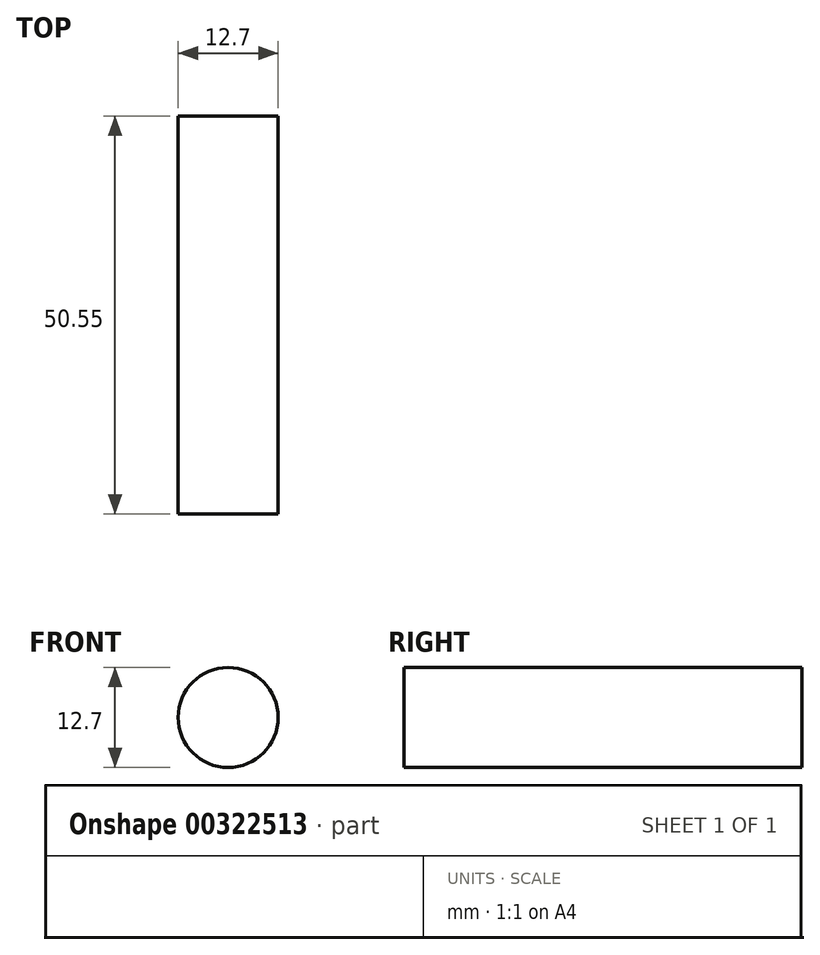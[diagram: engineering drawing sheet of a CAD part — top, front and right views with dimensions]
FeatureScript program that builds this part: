
annotation { "Feature Type Name" : "Feature", "Feature Type Description" : "" }
export const myFeature = defineFeature(function(context is Context, id is Id, definition is map)
    precondition{}
    {
        {
            var Q0;
            Q0=qCreatedBy(makeId("Front.planeOp"),FACE);
            var sketch = newSketch(context, id + "F0", { "sketchPlane" : qUnion([Q0])});
            skLineSegment(sketch, "E0.top", {"start": v(0, -50.8) * mm, "end": v(50.8, -50.8) * mm});
            skLineSegment(sketch, "E0.left", {"start": v(0, 0) * mm, "end": v(0, -31.4) * mm});
            skLineSegment(sketch, "E0.right", {"start": v(50.8, 0) * mm, "end": v(50.8, -50.8) * mm});
            skLineSegment(sketch, "E1", {"start": v(0, 0) * mm, "end": v(25.4, 44) * mm});
            skLineSegment(sketch, "E2", {"start": v(50.8, 0) * mm, "end": v(25.4, 44) * mm});
            skPoint(sketch, "E3.end.orphan", {"position": v(50.8, -31.75) * mm});
            skPoint(sketch, "E4.end.orphan", {"position": v(0, -31.4) * mm});
            skCircle(sketch, "E5", {"center": v(19.05, -31.75) * mm, "radius": 6.35 * mm});
            skPoint(sketch, "E6.orphan", {"position": v(0, -31.75) * mm});
            skPoint(sketch, "E7.end.orphan", {"position": v(19.05, -32.1) * mm});
            skLineSegment(sketch, "E8.trimOffspring", {"start": v(0, -31.75) * mm, "end": v(0, -50.8) * mm});
            skSolve(sketch);
        }
        {
            var Q0;
            Q0 = qSketchRegion(id + "F0", true);
            extrude(context, id + "F1", {"entities" : qUnion([Q0]), "depth" : 50.55 * mm});
        }
    });
